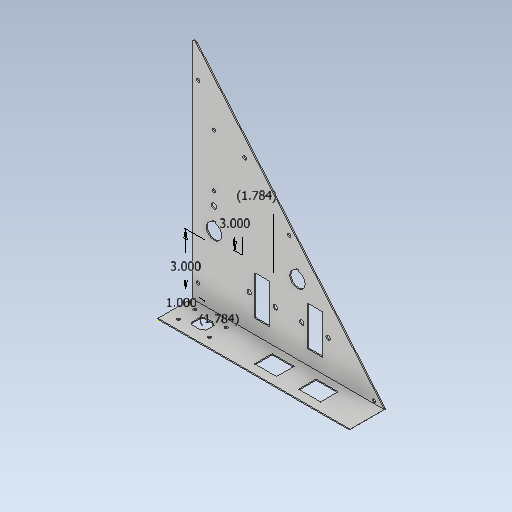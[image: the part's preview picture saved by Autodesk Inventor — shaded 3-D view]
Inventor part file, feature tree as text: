
AUTODESK INVENTOR PART (.ipt)
format: ipt  version: 2021 (Build 250183000, 183)  size: 402,944 bytes
history: native  units: in
note: dims shown in document units (in); Inventor stores cm internally (conversion verified against a paired STEP export)
features: extrude x8, sketch x8, fillet x2, other x2
ambient origin geometry x8: Origin, YZ Plane, XZ Plane, XY Plane, X Axis, Y Axis, Z Axis, Center Point
bodies: Solid1 (feature_tree)
feature tree (20):
  extrude  "Extrusion1"  Depth=0.063in
  extrude  "Extrusion3"  Depth=0.126in
  sketch  "Sketch4"  dims[d27=0.2559in d29=0.256in d30=0.748in d31=0.2559in d33=0.256in d34=0.748in d43=0.875in d44=0.07in d45=0.126in]
  extrude  "Extrusion5"  Depth=0.85in
  extrude  "Extrusion6"  Depth=1.0in TaperAngle=0.0deg
  extrude  "Extrusion7"  Depth=1.0in
  extrude  "Extrusion8"  Depth=0.35in
  extrude  "Extrusion9"  Depth=0.5in
  extrude  "Extrusion10"  Depth=0.5in
  sketch  "Sketch10"  dims[d58=10.0in d59=0.35in]
  sketch  "Sketch11"  dims[d60=9.0in d61=0.35in d64=0.19in d65=0.19in d66=0.19in d67=0.25in d68=0.0in d69=1.94in d70=13.358in d71=0.06in d72=0.0in d78=0.168in d79=0.39in d80=0.168in d81=0.3878in d82=0.168in d83=90.0deg d84=0.168in d85=0.3878in d86=0.0355in d87=0.1in d88=0.495in d96=0.17in d97=0.17in d98=0.17in d99=0.17in d100=0.06in d101=0.0in d108=0.25in d109=0.0in d114=3.0in d121=1.784in d126=3.0in d127=1.7838in d146=1.0in d149=0.125in d152=0.05in d154=0.3125in d155=5.25in d156=1.25in d161=5.0in d162=0.5in d163=1.0in d164=1.25in d165=1.25in d166=1.25in d175=7.5in d176=0.35in d177=0.19in d181=3.0in d182=8.5in d183=0.2188in d102=0.5in d103=0.0344in]
  fillet  "Fillet1"  Radius=0.19in
  fillet  "Fillet4"  Radius=0.19in
  sketch  "Sketch1"  dims[d2=0.063in d3=0.0in d4=0.875in]
  sketch  "Sketch3"  dims[d15=1.0in d16=0.0in]
  sketch  "Sketch5"  dims[d49=1.0in d50=0.0in d51=0.85in]
  sketch  "Sketch6"  dims[d53=0.85in d54=1.0in d55=0.0in]
  sketch  "Sketch7"  dims[d56=1.0in d57=0.35in]
  other  "Image1"
  other  "Image2"
